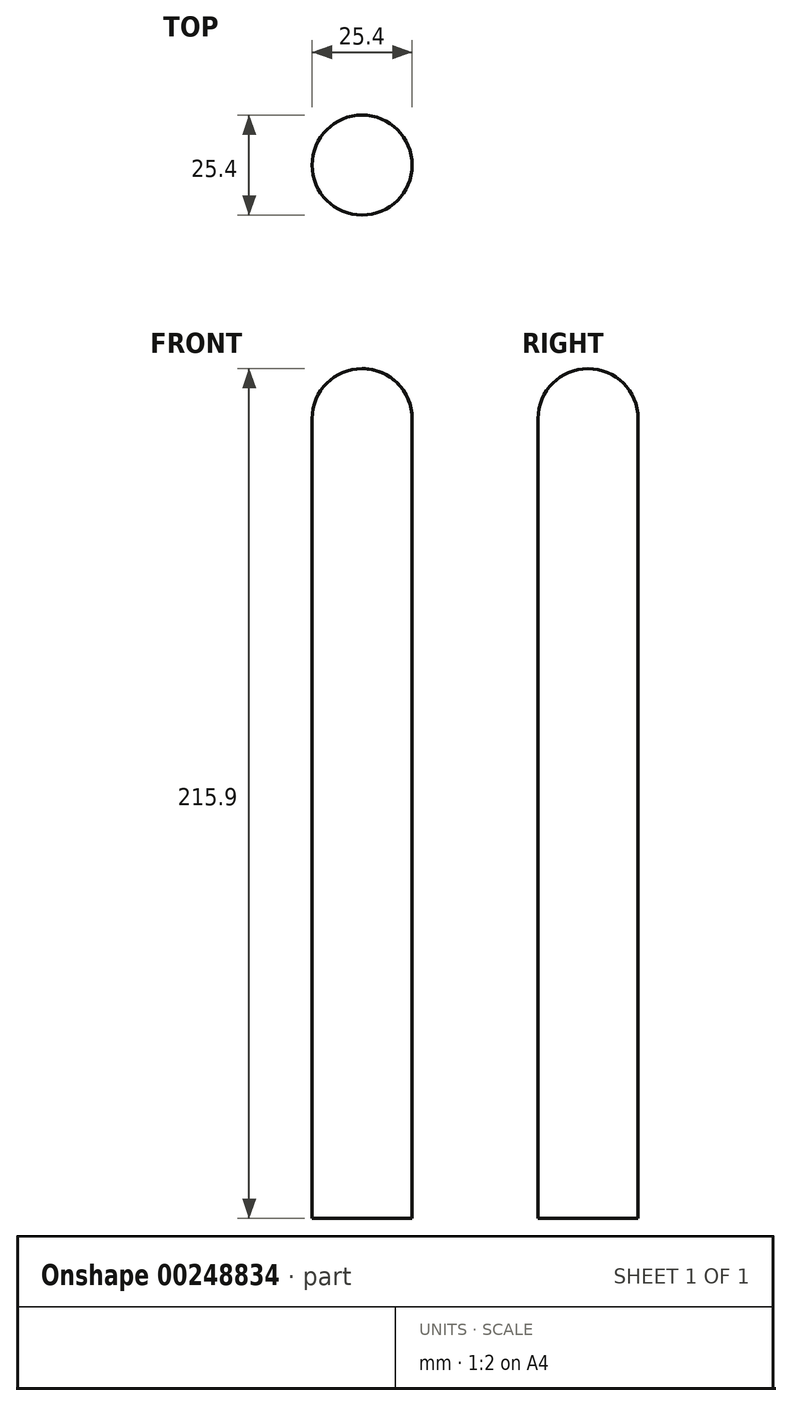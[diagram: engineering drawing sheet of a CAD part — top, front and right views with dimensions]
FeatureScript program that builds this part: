
annotation { "Feature Type Name" : "Feature", "Feature Type Description" : "" }
export const myFeature = defineFeature(function(context is Context, id is Id, definition is map)
    precondition{}
    {
        {
            var Q0;
            Q0=qCreatedBy(makeId("Top.planeOp"),FACE);
            var sketch = newSketch(context, id + "F0", { "sketchPlane" : qUnion([Q0])});
            skCircle(sketch, "E0", {"center": v(0, 0) * mm, "radius": 12.7 * mm});
            skSolve(sketch);
        }
        {
            var Q0;
            Q0=makeQuery(id+"F0.imprint","IMPRINT",FACE,{"disambiguationData":[TD([[makeQuery(id+"F0.imprint","IMPRINT",EDGE,{"derivedFrom":sQuery(id+"F0.wireOp",EDGE,"E0")}),1.0]])]});
            extrude(context, id + "F1", {"entities" : qUnion([Q0]), "depth" : 203.2 * mm});
        }
        {
            var Q0;
            Q0=qCreatedBy(makeId("Front.planeOp"),FACE);
            var sketch = newSketch(context, id + "F2", { "sketchPlane" : qUnion([Q0])});
            skLineSegment(sketch, "E1", {"start": v(0, 203.2) * mm, "end": v(0, 215.9) * mm});
            skLineSegment(sketch, "E2", {"start": v(0, 203.2) * mm, "end": v(12.7, 203.2) * mm});
            skArc(sketch, "E3", {"start": v(12.7, 203.2) * mm, "mid": v(8.98, 212.18) * mm, "end": v(0, 215.9) * mm});
            skSolve(sketch);
        }
        {
            var Q0;
            Q0=makeQuery(id+"F2.imprint","IMPRINT",FACE,{"disambiguationData":[TD([[makeQuery(id+"F2.imprint","IMPRINT",EDGE,{"derivedFrom":sQuery(id+"F2.wireOp",EDGE,"E1")}),-1.0]])]});
            var Q1;
            Q1=sQuery(id+"F2.wireOp",EDGE,"E1");
            revolve(context, id + "F3", {"operationType" : NewBodyOperationType.ADD, "entities" : qUnion([Q0]), "axis" : qUnion([Q1]), "revolveType" : RevolveType.FULL});
        }
    });
